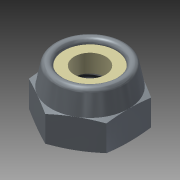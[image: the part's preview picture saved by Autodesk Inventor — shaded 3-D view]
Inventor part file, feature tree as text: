
AUTODESK INVENTOR PART (.ipt)
format: ipt  version: 2014 (Build 180170000, 170)  size: 190,976 bytes
history: native  units: mm (DEFAULTED — no unit token found)
features: sketch x5, extrude x2, revolve x2, other x1, plane x1, thread x1
ambient origin geometry x8: Origin, YZ Plane, XZ Plane, XY Plane, X Axis, Y Axis, Z Axis, Center Point
bodies: Solid1 (feature_tree)
feature tree (12):
  other  "Hexagon_flats_join1"
  extrude  "Extrusion1"  Depth=25.4mm TaperAngle=0.0deg
  revolve  "Revolution1"  Angle=90.0deg
  plane  "Work Plane1"
  extrude  "Extrusion2"  Depth=1.566333mm
  revolve  "Revolution2"  Angle=15.0deg
  thread  "Thread1"  [1 undecoded]
  sketch  "Sketch1"  dims[d0=9.525mm d3=25.4mm d4=0.0mm]
  sketch  "Sketch2"  dims[d5=13.788101mm d7=90.0deg]
  sketch  "Sketch3"  dims[d9=25.4mm d10=0.0mm d11=1.566333mm]
  sketch  "Sketch4"  dims[d12=15.0deg d13=15.0deg d14=9.525mm]
  sketch  "Sketch5"  dims[d15=90.0deg d16=25.4mm d17=0.0mm]
note: 1 required parameter value undecoded (feature->parameter linkage not recoverable at this tier; creation-order binding heuristic only, values carry confidence <= 0.55)
